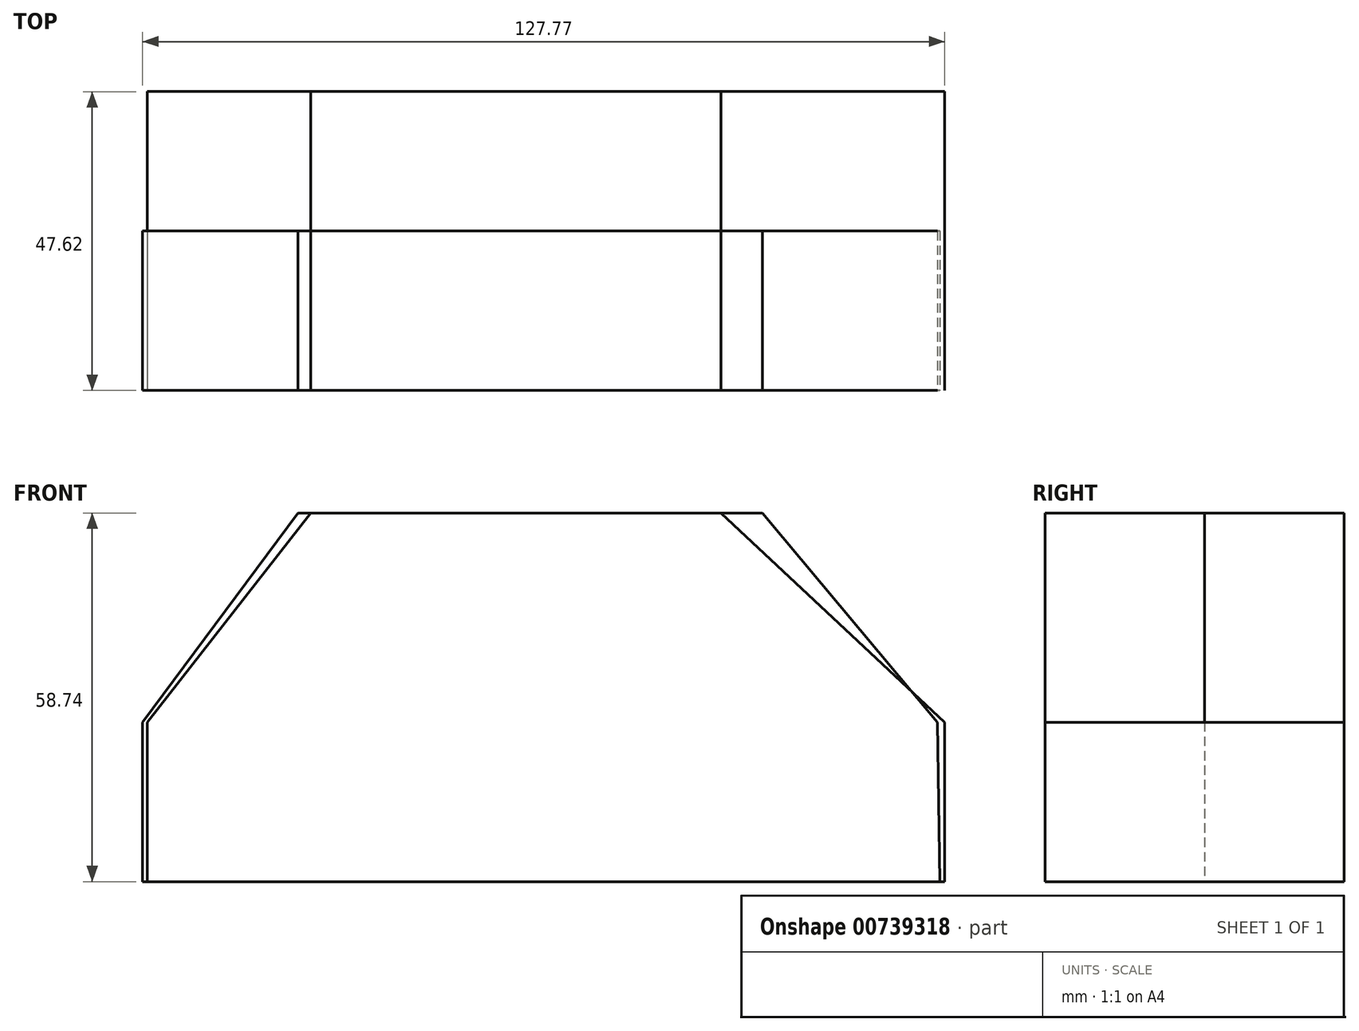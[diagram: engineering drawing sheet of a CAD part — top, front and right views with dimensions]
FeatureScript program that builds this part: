
annotation { "Feature Type Name" : "Feature", "Feature Type Description" : "" }
export const myFeature = defineFeature(function(context is Context, id is Id, definition is map)
    precondition{}
    {
        {
            var Q0;
            Q0=qCreatedBy(makeId("Front.planeOp"),FACE);
            var sketch = newSketch(context, id + "F0", { "sketchPlane" : qUnion([Q0])});
            skLineSegment(sketch, "E0.top", {"start": v(63.5, -58.74) * mm, "end": v(-63.5, -58.74) * mm});
            skPoint(sketch, "E0.middle", {"position": v(0, 0) * mm});
            skLineSegment(sketch, "E1", {"start": v(-63.5, -58.74) * mm, "end": v(-63.5, -33.34) * mm});
            skLineSegment(sketch, "E2", {"start": v(-63.5, -33.34) * mm, "end": v(-38.74, 0) * mm});
            skLineSegment(sketch, "E3", {"start": v(-38.74, 0) * mm, "end": v(35.26, 0) * mm});
            skLineSegment(sketch, "E4", {"start": v(35.26, 0) * mm, "end": v(63.08, -33.34) * mm});
            skLineSegment(sketch, "E5", {"start": v(63.08, -33.34) * mm, "end": v(63.5, -58.74) * mm});
            skSolve(sketch);
        }
        {
            var Q0;
            Q0 = qSketchRegion(id + "F0", true);
            extrude(context, id + "F1", {"entities" : qUnion([Q0]), "oppositeDirection" : true, "depth" : 25.4 * mm, "offsetDistance" : 25.4 * mm});
        }
        {
            var Q0;
            Q0=qCreatedBy(makeId("Front.planeOp"),FACE);
            var sketch = newSketch(context, id + "F2", { "sketchPlane" : qUnion([Q0])});
            skLineSegment(sketch, "E6", {"start": v(-62.73, -58.74) * mm, "end": v(64.27, -58.74) * mm});
            skLineSegment(sketch, "E7", {"start": v(64.27, -58.74) * mm, "end": v(64.27, -33.34) * mm});
            skLineSegment(sketch, "E8", {"start": v(64.27, -33.34) * mm, "end": v(28.65, 0) * mm});
            skLineSegment(sketch, "E9", {"start": v(28.65, 0) * mm, "end": v(-36.7, 0) * mm});
            skLineSegment(sketch, "E10", {"start": v(-36.7, 0) * mm, "end": v(-62.73, -33.34) * mm});
            skLineSegment(sketch, "E11", {"start": v(-62.73, -33.34) * mm, "end": v(-62.73, -58.74) * mm});
            skSolve(sketch);
        }
        {
            var Q0;
            Q0=makeQuery(id+"F2.imprint","IMPRINT",FACE,{"disambiguationData":[TD([[makeQuery(id+"F2.imprint","IMPRINT",EDGE,{"derivedFrom":sQuery(id+"F2.wireOp",EDGE,"E6")}),1.0]])]});
            extrude(context, id + "F3", {"entities" : qUnion([Q0]), "oppositeDirection" : true, "depth" : 47.62 * mm, "offsetDistance" : 25.4 * mm});
        }
    });
